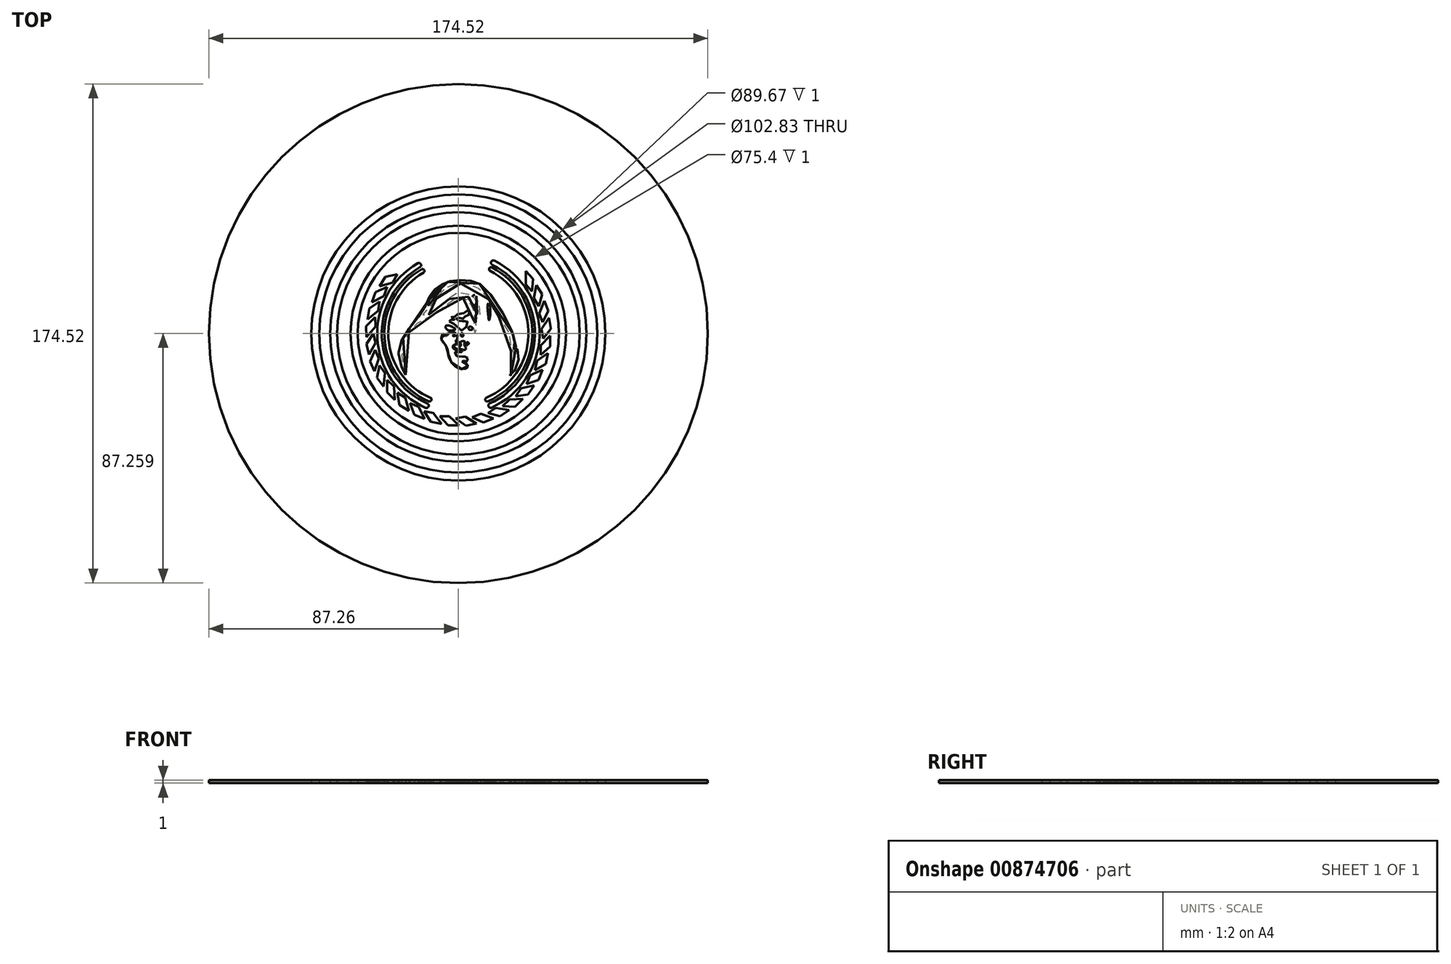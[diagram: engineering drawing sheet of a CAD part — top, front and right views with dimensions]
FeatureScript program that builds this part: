
annotation { "Feature Type Name" : "Feature", "Feature Type Description" : "" }
export const myFeature = defineFeature(function(context is Context, id is Id, definition is map)
    precondition{}
    {
        {
            var Q0;
            Q0=qCreatedBy(makeId("Top.planeOp"),FACE);
            var sketch = newSketch(context, id + "F0", { "sketchPlane" : qUnion([Q0])});
            skLineSegment(sketch, "E0", {"start": v(51.5, -19.06) * mm, "end": v(51.41, -19.06) * mm});
            skCircle(sketch, "E1", {"center": v(0, -19.06) * mm, "radius": 51.41 * mm});
            skCircle(sketch, "E2", {"center": v(0, -19.06) * mm, "radius": 48.62 * mm});
            skCircle(sketch, "E3", {"center": v(0, -19.06) * mm, "radius": 44.83 * mm});
            skCircle(sketch, "E4", {"center": v(0, -19.06) * mm, "radius": 42.44 * mm});
            skCircle(sketch, "E5", {"center": v(0, -19.06) * mm, "radius": 37.7 * mm});
            skCircle(sketch, "E6", {"center": v(0, -19.06) * mm, "radius": 35.2 * mm});
            skPoint(sketch, "E7.orphan", {"position": v(0, -69.88) * mm});
            skLineSegment(sketch, "E8.trimOffspring", {"start": v(51.41, -19.06) * mm, "end": v(51.5, -19.06) * mm});
            skPoint(sketch, "E9.orphan", {"position": v(0, 31.76) * mm});
            skLineSegment(sketch, "E10", {"start": v(25.81, -4.35) * mm, "end": v(23.57, -1.93) * mm});
            skLineSegment(sketch, "E11", {"start": v(23.57, -1.93) * mm, "end": v(23.57, 2.8) * mm});
            skLineSegment(sketch, "E12", {"start": v(23.57, 2.8) * mm, "end": v(26.17, 0) * mm});
            skLineSegment(sketch, "E13", {"start": v(26.17, 0) * mm, "end": v(25.81, -4.35) * mm});
            skLineSegment(sketch, "E14.1.0", {"start": v(27.32, -2.12) * mm, "end": v(29.33, -5.36) * mm});
            skLineSegment(sketch, "E14.1.1", {"start": v(26.41, -6.76) * mm, "end": v(27.32, -2.12) * mm});
            skLineSegment(sketch, "E14.1.2", {"start": v(29.33, -5.36) * mm, "end": v(28.15, -9.56) * mm});
            skLineSegment(sketch, "E14.1.3", {"start": v(28.15, -9.56) * mm, "end": v(26.41, -6.76) * mm});
            skLineSegment(sketch, "E14.2.0", {"start": v(30.05, -7.66) * mm, "end": v(31.41, -11.23) * mm});
            skLineSegment(sketch, "E14.2.1", {"start": v(28.28, -12.04) * mm, "end": v(30.05, -7.66) * mm});
            skLineSegment(sketch, "E14.2.2", {"start": v(31.41, -11.23) * mm, "end": v(29.45, -15.13) * mm});
            skLineSegment(sketch, "E14.2.3", {"start": v(29.45, -15.13) * mm, "end": v(28.28, -12.04) * mm});
            skLineSegment(sketch, "E14.3.0", {"start": v(31.68, -13.62) * mm, "end": v(32.33, -17.39) * mm});
            skLineSegment(sketch, "E14.3.1", {"start": v(29.1, -17.58) * mm, "end": v(31.68, -13.62) * mm});
            skLineSegment(sketch, "E14.3.2", {"start": v(32.33, -17.39) * mm, "end": v(29.66, -20.84) * mm});
            skLineSegment(sketch, "E14.3.3", {"start": v(29.66, -20.84) * mm, "end": v(29.1, -17.58) * mm});
            skLineSegment(sketch, "E14.4.0", {"start": v(32.14, -19.79) * mm, "end": v(32.05, -23.6) * mm});
            skLineSegment(sketch, "E14.4.1", {"start": v(28.84, -23.18) * mm, "end": v(32.14, -19.79) * mm});
            skLineSegment(sketch, "E14.4.2", {"start": v(32.05, -23.6) * mm, "end": v(28.77, -26.48) * mm});
            skLineSegment(sketch, "E14.4.3", {"start": v(28.77, -26.48) * mm, "end": v(28.84, -23.18) * mm});
            skLineSegment(sketch, "E14.5.0", {"start": v(31.4, -25.92) * mm, "end": v(30.6, -29.66) * mm});
            skLineSegment(sketch, "E14.5.1", {"start": v(27.52, -28.62) * mm, "end": v(31.4, -25.92) * mm});
            skLineSegment(sketch, "E14.5.2", {"start": v(30.6, -29.66) * mm, "end": v(26.82, -31.85) * mm});
            skLineSegment(sketch, "E14.5.3", {"start": v(26.82, -31.85) * mm, "end": v(27.52, -28.62) * mm});
            skLineSegment(sketch, "E14.6.0", {"start": v(29.5, -31.8) * mm, "end": v(28, -35.31) * mm});
            skLineSegment(sketch, "E14.6.1", {"start": v(25.18, -33.71) * mm, "end": v(29.5, -31.8) * mm});
            skLineSegment(sketch, "E14.6.2", {"start": v(28, -35.31) * mm, "end": v(23.87, -36.75) * mm});
            skLineSegment(sketch, "E14.6.3", {"start": v(23.87, -36.75) * mm, "end": v(25.18, -33.71) * mm});
            skLineSegment(sketch, "E14.7.0", {"start": v(26.52, -37.22) * mm, "end": v(24.37, -40.37) * mm});
            skLineSegment(sketch, "E14.7.1", {"start": v(21.91, -38.26) * mm, "end": v(26.52, -37.22) * mm});
            skLineSegment(sketch, "E14.7.2", {"start": v(24.37, -40.37) * mm, "end": v(20.05, -40.99) * mm});
            skLineSegment(sketch, "E14.7.3", {"start": v(20.05, -40.99) * mm, "end": v(21.91, -38.26) * mm});
            skLineSegment(sketch, "E14.8.0", {"start": v(22.56, -41.96) * mm, "end": v(19.84, -44.64) * mm});
            skLineSegment(sketch, "E14.8.1", {"start": v(17.83, -42.1) * mm, "end": v(22.56, -41.96) * mm});
            skLineSegment(sketch, "E14.8.2", {"start": v(19.84, -44.64) * mm, "end": v(15.48, -44.42) * mm});
            skLineSegment(sketch, "E14.8.3", {"start": v(15.48, -44.42) * mm, "end": v(17.83, -42.1) * mm});
            skLineSegment(sketch, "E14.9.0", {"start": v(17.76, -45.86) * mm, "end": v(14.58, -47.97) * mm});
            skLineSegment(sketch, "E14.9.1", {"start": v(13.1, -45.1) * mm, "end": v(17.76, -45.86) * mm});
            skLineSegment(sketch, "E14.9.2", {"start": v(14.58, -47.97) * mm, "end": v(10.34, -46.91) * mm});
            skLineSegment(sketch, "E14.9.3", {"start": v(10.34, -46.91) * mm, "end": v(13.1, -45.1) * mm});
            skLineSegment(sketch, "E14.10.0", {"start": v(12.3, -48.76) * mm, "end": v(8.77, -50.22) * mm});
            skLineSegment(sketch, "E14.10.1", {"start": v(7.87, -47.12) * mm, "end": v(12.3, -48.76) * mm});
            skLineSegment(sketch, "E14.10.2", {"start": v(8.77, -50.22) * mm, "end": v(4.82, -48.38) * mm});
            skLineSegment(sketch, "E14.10.3", {"start": v(4.82, -48.38) * mm, "end": v(7.87, -47.12) * mm});
            skLineSegment(sketch, "E14.11.0", {"start": v(6.39, -50.56) * mm, "end": v(2.65, -51.33) * mm});
            skLineSegment(sketch, "E14.11.1", {"start": v(2.35, -48.1) * mm, "end": v(6.39, -50.56) * mm});
            skLineSegment(sketch, "E14.11.2", {"start": v(2.65, -51.33) * mm, "end": v(-0.88, -48.76) * mm});
            skLineSegment(sketch, "E14.11.3", {"start": v(-0.88, -48.76) * mm, "end": v(2.35, -48.1) * mm});
            skLineSegment(sketch, "E14.12.0", {"start": v(0.24, -51.2) * mm, "end": v(-3.58, -51.24) * mm});
            skLineSegment(sketch, "E14.12.1", {"start": v(-3.25, -48.02) * mm, "end": v(0.24, -51.2) * mm});
            skLineSegment(sketch, "E14.12.2", {"start": v(-3.58, -51.24) * mm, "end": v(-6.55, -48.04) * mm});
            skLineSegment(sketch, "E14.12.3", {"start": v(-6.55, -48.04) * mm, "end": v(-3.25, -48.02) * mm});
            skLineSegment(sketch, "E14.13.0", {"start": v(-5.92, -50.66) * mm, "end": v(-9.67, -49.96) * mm});
            skLineSegment(sketch, "E14.13.1", {"start": v(-8.73, -46.86) * mm, "end": v(-5.92, -50.66) * mm});
            skLineSegment(sketch, "E14.13.2", {"start": v(-9.67, -49.96) * mm, "end": v(-11.98, -46.25) * mm});
            skLineSegment(sketch, "E14.13.3", {"start": v(-11.98, -46.25) * mm, "end": v(-8.73, -46.86) * mm});
            skLineSegment(sketch, "E14.14.0", {"start": v(-11.85, -48.94) * mm, "end": v(-15.4, -47.54) * mm});
            skLineSegment(sketch, "E14.14.1", {"start": v(-13.89, -44.67) * mm, "end": v(-11.85, -48.94) * mm});
            skLineSegment(sketch, "E14.14.2", {"start": v(-15.4, -47.54) * mm, "end": v(-16.96, -43.46) * mm});
            skLineSegment(sketch, "E14.14.3", {"start": v(-16.96, -43.46) * mm, "end": v(-13.89, -44.67) * mm});
            skLineSegment(sketch, "E14.15.0", {"start": v(-17.35, -46.12) * mm, "end": v(-20.57, -44.06) * mm});
            skLineSegment(sketch, "E14.15.1", {"start": v(-18.54, -41.54) * mm, "end": v(-17.35, -46.12) * mm});
            skLineSegment(sketch, "E14.15.2", {"start": v(-20.57, -44.06) * mm, "end": v(-21.31, -39.76) * mm});
            skLineSegment(sketch, "E14.15.3", {"start": v(-21.31, -39.76) * mm, "end": v(-18.54, -41.54) * mm});
            skLineSegment(sketch, "E14.16.0", {"start": v(-22.21, -42.3) * mm, "end": v(-24.97, -39.66) * mm});
            skLineSegment(sketch, "E14.16.1", {"start": v(-22.5, -37.58) * mm, "end": v(-22.21, -42.3) * mm});
            skLineSegment(sketch, "E14.16.2", {"start": v(-24.97, -39.66) * mm, "end": v(-24.88, -35.3) * mm});
            skLineSegment(sketch, "E14.16.3", {"start": v(-24.88, -35.3) * mm, "end": v(-22.5, -37.58) * mm});
            skLineSegment(sketch, "E14.17.0", {"start": v(-26.25, -37.62) * mm, "end": v(-28.46, -34.5) * mm});
            skLineSegment(sketch, "E14.17.1", {"start": v(-25.62, -32.93) * mm, "end": v(-26.25, -37.62) * mm});
            skLineSegment(sketch, "E14.17.2", {"start": v(-28.46, -34.5) * mm, "end": v(-27.53, -30.23) * mm});
            skLineSegment(sketch, "E14.17.3", {"start": v(-27.53, -30.23) * mm, "end": v(-25.62, -32.93) * mm});
            skLineSegment(sketch, "E14.18.0", {"start": v(-29.31, -32.25) * mm, "end": v(-30.88, -28.77) * mm});
            skLineSegment(sketch, "E14.18.1", {"start": v(-27.8, -27.77) * mm, "end": v(-29.31, -32.25) * mm});
            skLineSegment(sketch, "E14.18.2", {"start": v(-30.88, -28.77) * mm, "end": v(-29.16, -24.76) * mm});
            skLineSegment(sketch, "E14.18.3", {"start": v(-29.16, -24.76) * mm, "end": v(-27.8, -27.77) * mm});
            skLineSegment(sketch, "E14.19.0", {"start": v(-31.3, -26.4) * mm, "end": v(-32.17, -22.68) * mm});
            skLineSegment(sketch, "E14.19.1", {"start": v(-28.96, -22.29) * mm, "end": v(-31.3, -26.4) * mm});
            skLineSegment(sketch, "E14.19.2", {"start": v(-32.17, -22.68) * mm, "end": v(-29.71, -19.07) * mm});
            skLineSegment(sketch, "E14.19.3", {"start": v(-29.71, -19.07) * mm, "end": v(-28.96, -22.29) * mm});
            skLineSegment(sketch, "E14.20.0", {"start": v(-32.12, -20.27) * mm, "end": v(-32.27, -16.45) * mm});
            skLineSegment(sketch, "E14.20.1", {"start": v(-29.04, -16.68) * mm, "end": v(-32.12, -20.27) * mm});
            skLineSegment(sketch, "E14.20.2", {"start": v(-32.27, -16.45) * mm, "end": v(-29.16, -13.39) * mm});
            skLineSegment(sketch, "E14.20.3", {"start": v(-29.16, -13.39) * mm, "end": v(-29.04, -16.68) * mm});
            skLineSegment(sketch, "E14.21.0", {"start": v(-31.76, -14.1) * mm, "end": v(-31.17, -10.33) * mm});
            skLineSegment(sketch, "E14.21.1", {"start": v(-28.05, -11.17) * mm, "end": v(-31.76, -14.1) * mm});
            skLineSegment(sketch, "E14.21.2", {"start": v(-31.17, -10.33) * mm, "end": v(-27.54, -7.9) * mm});
            skLineSegment(sketch, "E14.21.3", {"start": v(-27.54, -7.9) * mm, "end": v(-28.05, -11.17) * mm});
            skLineSegment(sketch, "E14.22.0", {"start": v(-30.22, -8.11) * mm, "end": v(-28.92, -4.52) * mm});
            skLineSegment(sketch, "E14.22.1", {"start": v(-26.02, -5.95) * mm, "end": v(-30.22, -8.11) * mm});
            skLineSegment(sketch, "E14.22.2", {"start": v(-28.92, -4.52) * mm, "end": v(-24.9, -2.84) * mm});
            skLineSegment(sketch, "E14.22.3", {"start": v(-24.9, -2.84) * mm, "end": v(-26.02, -5.95) * mm});
            skLineSegment(sketch, "E14.23.0", {"start": v(-27.57, -2.53) * mm, "end": v(-25.6, 0.75) * mm});
            skLineSegment(sketch, "E14.23.1", {"start": v(-23.03, -1.21) * mm, "end": v(-27.57, -2.53) * mm});
            skLineSegment(sketch, "E14.23.2", {"start": v(-25.6, 0.75) * mm, "end": v(-21.33, 1.62) * mm});
            skLineSegment(sketch, "E14.23.3", {"start": v(-21.33, 1.62) * mm, "end": v(-23.03, -1.21) * mm});
            skLineSegment(sketch, "E14.29.1", {"start": v(7.04, 9.21) * mm, "end": v(7.02, 9.24) * mm});
            skPoint(sketch, "E15.orphan", {"position": v(4, 12.83) * mm});
            skFitSpline(sketch, "E16", {"points": [v(-18.39, -33.56) * mm, v(-19.66, -25.5) * mm, v(-14.73, -15.7) * mm, v(-10.92, -13.68) * mm, v(-4.47, -9.3) * mm, v(-0.8, -6.74) * mm, v(2.17, -6.82) * mm, v(4.68, -9.37) * mm, v(5.66, -13.9) * mm, v(5.32, -17.84) * mm, v(5.92, -19) * mm, v(6.15, -17.17) * mm, v(6.52, -13.08) * mm, v(7.45, -13.57) * mm, v(6.06, -5.75) * mm, v(4.95, -6.02) * mm, v(5.6, -6.69) * mm, v(6.62, -12.2) * mm, v(5.99, -10.76) * mm, v(5.05, -8.4) * mm, v(3.05, -6.51) * mm, v(4.03, -5.87) * mm, v(0.48, -4.68) * mm, v(-3.2, -6.73) * mm, v(-3.04, -7.38) * mm, v(-4.83, -8.15) * mm, v(-6.38, -9.62) * mm, v(-12.76, -13.43) * mm, v(-8.95, -8.36) * mm, v(-7.28, -6.1) * mm, v(-3.31, -2.43) * mm, v(1.26, -1.5) * mm, v(6.21, -2.64) * mm, v(11.16, -8.07) * mm, v(12.59, -10.97) * mm, v(13.08, -10.44) * mm, v(13.74, -12.29) * mm, v(18.46, -21.07) * mm, v(18.29, -25.05) * mm, v(19.94, -26.59) * mm, v(17.83, -33.71) * mm, v(19.84, -31.85) * mm, v(20.97, -25.7) * mm, v(20.14, -23.92) * mm, v(19.66, -25.32) * mm, v(19.44, -23.45) * mm, v(19.66, -20.92) * mm, v(9.76, -3.66) * mm, v(3.94, -0.64) * mm, v(-1.85, -0.52) * mm, v(-6.1, -2.1) * mm, v(-9.28, -4.77) * mm, v(-11.43, -9.22) * mm, v(-17.67, -17.99) * mm, v(-20.93, -27) * mm, v(-18.39, -33.56) * mm]});
            skFitSpline(sketch, "E17", {"points": [v(-10.62, -9.08) * mm, v(-8.7, -4.93) * mm, v(-5.86, -2.81) * mm, v(-7.7, -5.74) * mm, v(-10.62, -9.08) * mm]});
            skFitSpline(sketch, "E18", {"points": [v(10.52, -8.54) * mm, v(11.16, -10.84) * mm, v(10.76, -14.35) * mm, v(10.48, -12.72) * mm, v(10.2, -9.66) * mm, v(10.52, -8.54) * mm]});
            skFitSpline(sketch, "E19", {"points": [v(1.2, -28.81) * mm, v(3.17, -29.96) * mm, v(2.9, -31.21) * mm, v(-0.68, -30.85) * mm, v(-3.44, -26.97) * mm, v(-3.6, -25.23) * mm, v(-4.95, -22.54) * mm, v(-6, -20.9) * mm, v(-5.21, -19.15) * mm, v(-4.46, -20.07) * mm, v(-3.83, -19.84) * mm, v(-3.9, -18.92) * mm, v(-3.24, -18.52) * mm, v(-2.54, -18.86) * mm, v(-1.14, -18.72) * mm, v(-2.21, -19.81) * mm, v(-1.84, -20.05) * mm, v(-0.44, -19.18) * mm, v(-0.22, -19.94) * mm, v(-0.58, -20.37) * mm, v(-0.56, -21.46) * mm, v(-1.03, -21.66) * mm, v(-0.6, -22.28) * mm, v(-1.16, -23.03) * mm, v(-1.84, -23.37) * mm, v(-1.34, -24.66) * mm, v(1.8, -25.21) * mm, v(1.28, -25.5) * mm, v(-0.5, -25.53) * mm, v(-1.47, -25.8) * mm, v(-0.9, -26.74) * mm, v(1.3, -27.4) * mm, v(3.3, -27.18) * mm, v(3.09, -27.84) * mm, v(3.84, -28.46) * mm, v(3.15, -28.93) * mm, v(2.25, -28.43) * mm, v(1.2, -28.81) * mm]});
            skFitSpline(sketch, "E20", {"points": [v(-3.17, -14.91) * mm, v(-0.6, -16.25) * mm, v(1.02, -18.01) * mm, v(3.37, -15.47) * mm, v(2.4, -14.6) * mm, v(1.69, -14.97) * mm, v(0.94, -14.54) * mm, v(-0.37, -14.54) * mm, v(-0.53, -13.42) * mm, v(1.05, -13.93) * mm, v(2.2, -13.4) * mm, v(2.6, -12.86) * mm, v(4.07, -12.27) * mm, v(3.32, -10.83) * mm, v(2.73, -11.55) * mm, v(-0.58, -12.43) * mm, v(-1.54, -13.4) * mm, v(-2.37, -13.34) * mm, v(-2.26, -13.74) * mm, v(-1.46, -13.74) * mm, v(-1.49, -14.3) * mm, v(-2.8, -14.3) * mm, v(-3.17, -14.91) * mm]});
            skFitSpline(sketch, "E21", {"points": [v(0.77, -22.1) * mm, v(0.85, -23.26) * mm, v(0.26, -24) * mm, v(1.73, -24.77) * mm, v(2.5, -24.6) * mm, v(2.45, -23.65) * mm, v(2.02, -23.1) * mm, v(2.32, -22.08) * mm, v(1.8, -21.73) * mm, v(0.77, -22.1) * mm]});
            skFitSpline(sketch, "E22", {"points": [v(2.75, -22.83) * mm, v(3.21, -22.1) * mm, v(3.63, -22.55) * mm, v(3.05, -23.1) * mm, v(2.75, -22.83) * mm]});
            skFitSpline(sketch, "E23", {"points": [v(-0.1, -22.13) * mm, v(-0.25, -22.92) * mm, v(0.29, -23) * mm, v(0.53, -22.59) * mm, v(0.34, -22.1) * mm, v(-0.1, -22.13) * mm]});
            skFitSpline(sketch, "E24", {"points": [v(1.17, -18.9) * mm, v(0.85, -19.71) * mm, v(1.43, -20.12) * mm, v(1.73, -19.54) * mm, v(1.17, -18.9) * mm]});
            skFitSpline(sketch, "E25", {"points": [v(-1.11, -17.52) * mm, v(-2.1, -16.73) * mm, v(-4, -16.23) * mm, v(-4.5, -16.8) * mm, v(-3.8, -17.78) * mm, v(-2.1, -17.99) * mm, v(-1.11, -17.52) * mm]});
            skFitSpline(sketch, "E26", {"points": [v(-3.17, -16.3) * mm, v(-2.86, -16.88) * mm, v(-1.75, -16.92) * mm], "startDerivative": vector(0.44, -1.6) * mm, "endDerivative": vector(2.32, 0.3) * mm});
            skFitSpline(sketch, "E27", {"points": [v(3.7, -16.86) * mm, v(4.48, -16.68) * mm, v(4.97, -17.36) * mm, v(4.47, -17.78) * mm, v(3.57, -17.44) * mm, v(3.7, -16.86) * mm]});
            skArc(sketch, "E28", {"start": v(9.73, -41.58) * mm, "mid": v(24.52, -19.76) * mm, "end": v(11, 2.87) * mm});
            skArc(sketch, "E29", {"start": v(10.32, -42.8) * mm, "mid": v(25.88, -19.8) * mm, "end": v(11.67, 4.05) * mm});
            skArc(sketch, "E30", {"start": v(11.75, 4.01) * mm, "mid": v(10.83, 3.8) * mm, "end": v(11, 2.87) * mm});
            skArc(sketch, "E31", {"start": v(-12.13, 2.26) * mm, "mid": v(-11.95, 3.17) * mm, "end": v(-12.84, 3.42) * mm});
            skArc(sketch, "E32", {"start": v(9.73, -41.58) * mm, "mid": v(9.47, -42.46) * mm, "end": v(10.32, -42.8) * mm});
            skArc(sketch, "E33", {"start": v(-10.33, -42.8) * mm, "mid": v(-9.53, -42.53) * mm, "end": v(-9.5, -41.68) * mm});
            skArc(sketch, "E34.trimOffspring", {"start": v(-12.13, 2.26) * mm, "mid": v(-24.49, -20.53) * mm, "end": v(-9.5, -41.68) * mm});
            skArc(sketch, "E35.trimOffspring", {"start": v(-12.84, 3.42) * mm, "mid": v(-25.85, -20.46) * mm, "end": v(-10.33, -42.8) * mm});
            skArc(sketch, "E36", {"start": v(10.8, -43.6) * mm, "mid": v(26.8, -19.61) * mm, "end": v(11.81, 5) * mm});
            skArc(sketch, "E37", {"start": v(11.5, -45.02) * mm, "mid": v(28.39, -19.77) * mm, "end": v(12.78, 6.3) * mm});
            skArc(sketch, "E38", {"start": v(-11.4, -45.07) * mm, "mid": v(-10.46, -44.67) * mm, "end": v(-10.62, -43.67) * mm});
            skArc(sketch, "E39", {"start": v(10.8, -43.6) * mm, "mid": v(10.59, -44.59) * mm, "end": v(11.5, -45.02) * mm});
            skArc(sketch, "E40", {"start": v(-13.18, 4.28) * mm, "mid": v(-13.2, 5.3) * mm, "end": v(-14.18, 5.54) * mm});
            skArc(sketch, "E41", {"start": v(12.78, 6.3) * mm, "mid": v(11.6, 6.18) * mm, "end": v(11.81, 5) * mm});
            skArc(sketch, "E42.trimOffspring", {"start": v(-13.18, 4.28) * mm, "mid": v(-26.77, -20.49) * mm, "end": v(-10.62, -43.67) * mm});
            skArc(sketch, "E43.trimOffspring", {"start": v(-14.18, 5.54) * mm, "mid": v(-28.35, -20.62) * mm, "end": v(-11.4, -45.07) * mm});
            skCircle(sketch, "E44", {"center": v(0, -19.06) * mm, "radius": 87.26 * mm});
            skSolve(sketch);
        }
        {
            var Q0;
            Q0=makeQuery(id+"F0.imprint","IMPRINT",FACE,{"disambiguationData":[TD([[makeQuery(id+"F0.imprint","IMPRINT",EDGE,{"derivedFrom":sQuery(id+"F0.wireOp",EDGE,"E1")}),-1.0]])]});
            var Q1;
            Q1=makeQuery(id+"F0.imprint","IMPRINT",FACE,{"disambiguationData":[TD([[makeQuery(id+"F0.imprint","IMPRINT",EDGE,{"derivedFrom":sQuery(id+"F0.wireOp",EDGE,"E2")}),1.0]])]});
            var Q2;
            Q2=makeQuery(id+"F0.imprint","IMPRINT",FACE,{"disambiguationData":[TD([[makeQuery(id+"F0.imprint","IMPRINT",EDGE,{"derivedFrom":sQuery(id+"F0.wireOp",EDGE,"E4")}),1.0]])]});
            var Q3;
            Q3=makeQuery(id+"F0.imprint","IMPRINT",FACE,{"disambiguationData":[TD([[makeQuery(id+"F0.imprint","IMPRINT",EDGE,{"derivedFrom":sQuery(id+"F0.wireOp",EDGE,"E6")}),1.0]])]});
            var Q4;
            Q4=makeQuery(id+"F0.imprint","IMPRINT",FACE,{"disambiguationData":[TD([[makeQuery(id+"F0.imprint","IMPRINT",EDGE,{"derivedFrom":sQuery(id+"F0.wireOp",EDGE,"E17")}),-1.0]])]});
            extrude(context, id + "F1", {"entities" : qUnion([Q0, Q1, Q2, Q3, Q4]), "depth" : 1 * mm, "offsetDistance" : 25 * mm});
        }
    });
